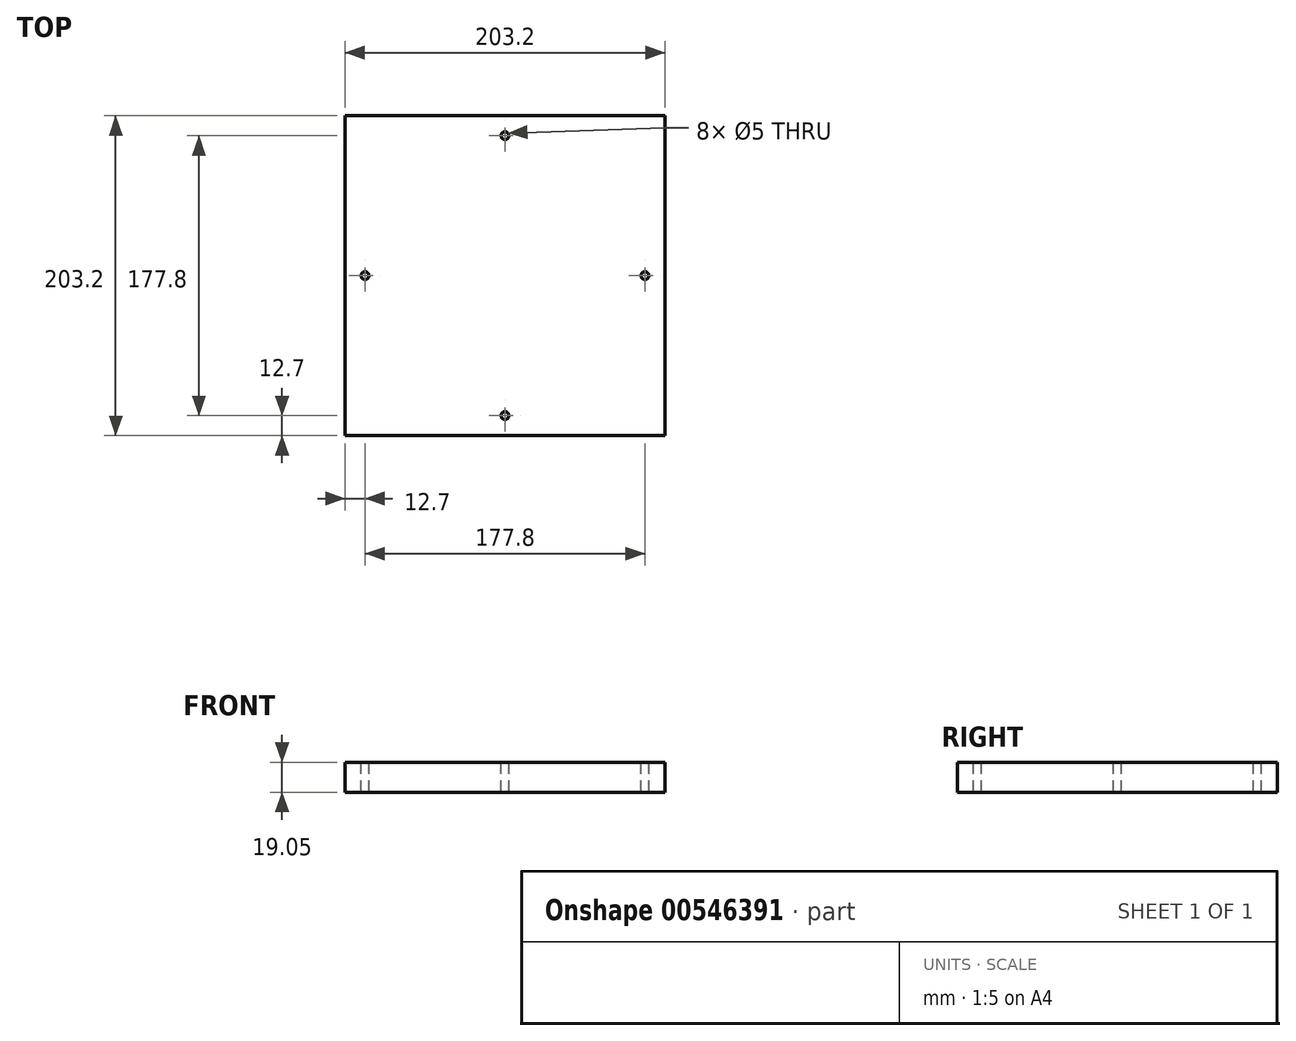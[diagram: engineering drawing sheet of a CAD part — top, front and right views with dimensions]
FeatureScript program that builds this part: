
annotation { "Feature Type Name" : "Feature", "Feature Type Description" : "" }
export const myFeature = defineFeature(function(context is Context, id is Id, definition is map)
    precondition{}
    {
        {
            var Q0;
            Q0=qCreatedBy(makeId("Top.planeOp"),FACE);
            var sketch = newSketch(context, id + "F0", { "sketchPlane" : qUnion([Q0])});
            skLineSegment(sketch, "E0.rect.bottom", {"start": v(101.6, -101.6) * mm, "end": v(-101.6, -101.6) * mm});
            skLineSegment(sketch, "E0.rect.top", {"start": v(101.6, 101.6) * mm, "end": v(-101.6, 101.6) * mm});
            skLineSegment(sketch, "E0.rect.left", {"start": v(101.6, -101.6) * mm, "end": v(101.6, 101.6) * mm});
            skLineSegment(sketch, "E0.rect.right", {"start": v(-101.6, -101.6) * mm, "end": v(-101.6, 101.6) * mm});
            skPoint(sketch, "E0.rect.middle", {"position": v(0, 0) * mm});
            skCircle(sketch, "E1", {"center": v(88.9, 88.9) * mm, "radius": 3.18 * mm});
            skCircle(sketch, "E2", {"center": v(-88.9, 88.9) * mm, "radius": 3.18 * mm});
            skCircle(sketch, "E3", {"center": v(-88.9, -88.9) * mm, "radius": 3.18 * mm});
            skCircle(sketch, "E4", {"center": v(88.9, -88.9) * mm, "radius": 3.18 * mm});
            skLineSegment(sketch, "E5.rect.bottom", {"start": v(88.9, 88.9) * mm, "end": v(-88.9, 88.9) * mm, "construction": true});
            skLineSegment(sketch, "E5.rect.top", {"start": v(88.9, -88.9) * mm, "end": v(-88.9, -88.9) * mm, "construction": true});
            skLineSegment(sketch, "E5.rect.left", {"start": v(88.9, 88.9) * mm, "end": v(88.9, -88.9) * mm, "construction": true});
            skLineSegment(sketch, "E5.rect.right", {"start": v(-88.9, 88.9) * mm, "end": v(-88.9, -88.9) * mm, "construction": true});
            skCircle(sketch, "E6", {"center": v(0, 19.05) * mm, "radius": 3.18 * mm});
            skPoint(sketch, "E7", {"position": v(-88.9, 0) * mm});
            skPoint(sketch, "E8", {"position": v(0, 88.9) * mm});
            skPoint(sketch, "E9", {"position": v(88.9, 0) * mm});
            skPoint(sketch, "E10", {"position": v(0, -88.9) * mm});
            skSolve(sketch);
        }
        {
            var Q0;
            Q0=qSketchRegion(id+"F0",true);
            var Q1;
            Q1=makeQuery(id+"F0.imprint","IMPRINT",FACE,{"disambiguationData":[TD([[makeQuery(id+"F0.imprint","IMPRINT",EDGE,{"derivedFrom":sQuery(id+"F0.wireOp",EDGE,"E3")}),1.0]])]});
            var Q2;
            Q2=makeQuery(id+"F0.imprint","IMPRINT",FACE,{"disambiguationData":[TD([[makeQuery(id+"F0.imprint","IMPRINT",EDGE,{"derivedFrom":sQuery(id+"F0.wireOp",EDGE,"E4")}),1.0]])]});
            var Q3;
            Q3=makeQuery(id+"F0.imprint","IMPRINT",FACE,{"disambiguationData":[TD([[makeQuery(id+"F0.imprint","IMPRINT",EDGE,{"derivedFrom":sQuery(id+"F0.wireOp",EDGE,"E6")}),1.0]])]});
            var Q4;
            Q4=makeQuery(id+"F0.imprint","IMPRINT",FACE,{"disambiguationData":[TD([[makeQuery(id+"F0.imprint","IMPRINT",EDGE,{"derivedFrom":sQuery(id+"F0.wireOp",EDGE,"E2")}),1.0]])]});
            var Q5;
            Q5=makeQuery(id+"F0.imprint","IMPRINT",FACE,{"disambiguationData":[TD([[makeQuery(id+"F0.imprint","IMPRINT",EDGE,{"derivedFrom":sQuery(id+"F0.wireOp",EDGE,"E1")}),1.0]])]});
            extrude(context, id + "F1", {"entities" : qUnion([Q0, Q1, Q2, Q3, Q4, Q5]), "depth" : 19.05 * mm, "offsetDistance" : 25.4 * mm});
        }
        {
            var Q0;
            Q0=makeQuery(id+"F1.opExtrude","CAP_FACE",FACE,{"disambiguationData":[OSD([sQuery(id+"F0.wireOp",EDGE,"E0.rect.bottom"),sQuery(id+"F0.wireOp",EDGE,"E0.rect.top"),sQuery(id+"F0.wireOp",EDGE,"E0.rect.left"),sQuery(id+"F0.wireOp",EDGE,"E0.rect.right"),sQuery(id+"F0.wireOp",EDGE,"E1"),sQuery(id+"F0.wireOp",EDGE,"E2"),sQuery(id+"F0.wireOp",EDGE,"E3"),sQuery(id+"F0.wireOp",EDGE,"E4"),sQuery(id+"F0.wireOp",EDGE,"E6")])],"isStart":false});
            var sketch = newSketch(context, id + "F2", { "sketchPlane" : qUnion([Q0])});
            skCircle(sketch, "E11", {"center": v(-88.9, 88.9) * mm, "radius": 5.08 * mm});
            skCircle(sketch, "E12", {"center": v(0, 19.05) * mm, "radius": 5.08 * mm});
            skCircle(sketch, "E13", {"center": v(88.9, 88.9) * mm, "radius": 5.08 * mm});
            skCircle(sketch, "E14", {"center": v(-88.9, -88.9) * mm, "radius": 5.08 * mm});
            skCircle(sketch, "E15", {"center": v(88.9, -88.9) * mm, "radius": 5.08 * mm});
            skPoint(sketch, "E16.0", {"position": v(0, 88.9) * mm});
            skPoint(sketch, "E16.1", {"position": v(0, -88.9) * mm});
            skPoint(sketch, "E16.2", {"position": v(88.9, 0) * mm});
            skPoint(sketch, "E16.3", {"position": v(-88.9, 0) * mm});
            skLineSegment(sketch, "E17.0", {"start": v(-88.9, 88.9) * mm, "end": v(-88.9, -88.9) * mm, "construction": true});
            skLineSegment(sketch, "E17.1", {"start": v(88.9, 88.9) * mm, "end": v(-88.9, 88.9) * mm, "construction": true});
            skLineSegment(sketch, "E17.2", {"start": v(88.9, 88.9) * mm, "end": v(88.9, -88.9) * mm, "construction": true});
            skLineSegment(sketch, "E17.3", {"start": v(88.9, -88.9) * mm, "end": v(-88.9, -88.9) * mm, "construction": true});
            skLineSegment(sketch, "E18", {"start": v(-88.9, 0) * mm, "end": v(88.9, 0) * mm, "construction": true});
            skLineSegment(sketch, "E19", {"start": v(0, 88.9) * mm, "end": v(0, -88.9) * mm, "construction": true});
            skPoint(sketch, "E20", {"position": v(-88.9, 71.12) * mm});
            skPoint(sketch, "E21", {"position": v(-71.12, 88.9) * mm});
            skPoint(sketch, "E22.MirrorP", {"position": v(71.12, 88.9) * mm});
            skPoint(sketch, "E23.MirrorP", {"position": v(88.9, 71.12) * mm});
            skPoint(sketch, "E24.MirrorP", {"position": v(88.9, -71.12) * mm});
            skPoint(sketch, "E25.MirrorP", {"position": v(71.12, -88.9) * mm});
            skPoint(sketch, "E26.MirrorP", {"position": v(-71.12, -88.9) * mm});
            skPoint(sketch, "E27.MirrorP", {"position": v(-88.9, -71.12) * mm});
            skSolve(sketch);
        }
        {
            var Q0;
            Q0=sQuery(id+"F2.wireOp",VERTEX,"E16.1");
            var Q1;
            Q1=sQuery(id+"F2.wireOp",VERTEX,"E16.2");
            var Q2;
            Q2=sQuery(id+"F2.wireOp",VERTEX,"E16.3");
            var Q3;
            Q3=sQuery(id+"F2.wireOp",VERTEX,"E16.0");
            var Q4;
            Q4=makeQuery(id+"F1.opExtrude","SWEPT_BODY",BODY,{"disambiguationData":[OSD([sQuery(id+"F0.wireOp",EDGE,"E0.rect.bottom"),sQuery(id+"F0.wireOp",EDGE,"E0.rect.top"),sQuery(id+"F0.wireOp",EDGE,"E0.rect.left"),sQuery(id+"F0.wireOp",EDGE,"E0.rect.right"),sQuery(id+"F0.wireOp",EDGE,"E1"),sQuery(id+"F0.wireOp",EDGE,"E2"),sQuery(id+"F0.wireOp",EDGE,"E3"),sQuery(id+"F0.wireOp",EDGE,"E4"),sQuery(id+"F0.wireOp",EDGE,"E6")])]});
            hole(context, id + "F3", {"style" : HoleStyle.SIMPLE, "endStyle" : HoleEndStyle.BLIND, "holeDiameter" : 5 * mm, "holeDepth" : 19.05 * mm, "isTappedThrough" : true, "tappedDepth" : 12.7 * mm, "tapClearance" : 3, "locations" : qUnion([Q0, Q1, Q2, Q3]), "scope" : qUnion([Q4])});
        }
        {
            var Q0;
            Q0=makeQuery(id+"F1.opExtrude","SWEPT_BODY",BODY,{"disambiguationData":[OSD([sQuery(id+"F0.wireOp",EDGE,"E0.rect.bottom"),sQuery(id+"F0.wireOp",EDGE,"E0.rect.top"),sQuery(id+"F0.wireOp",EDGE,"E0.rect.left"),sQuery(id+"F0.wireOp",EDGE,"E0.rect.right")])]});
            transform(context, id + "F4", {"entities" : qUnion([Q0]), "transformType" : TransformType.TRANSLATION_3D, "dx" : 0 * mm, "dy" : 0 * mm, "dz" : 0 * mm, "makeCopy" : true});
        }
    });
